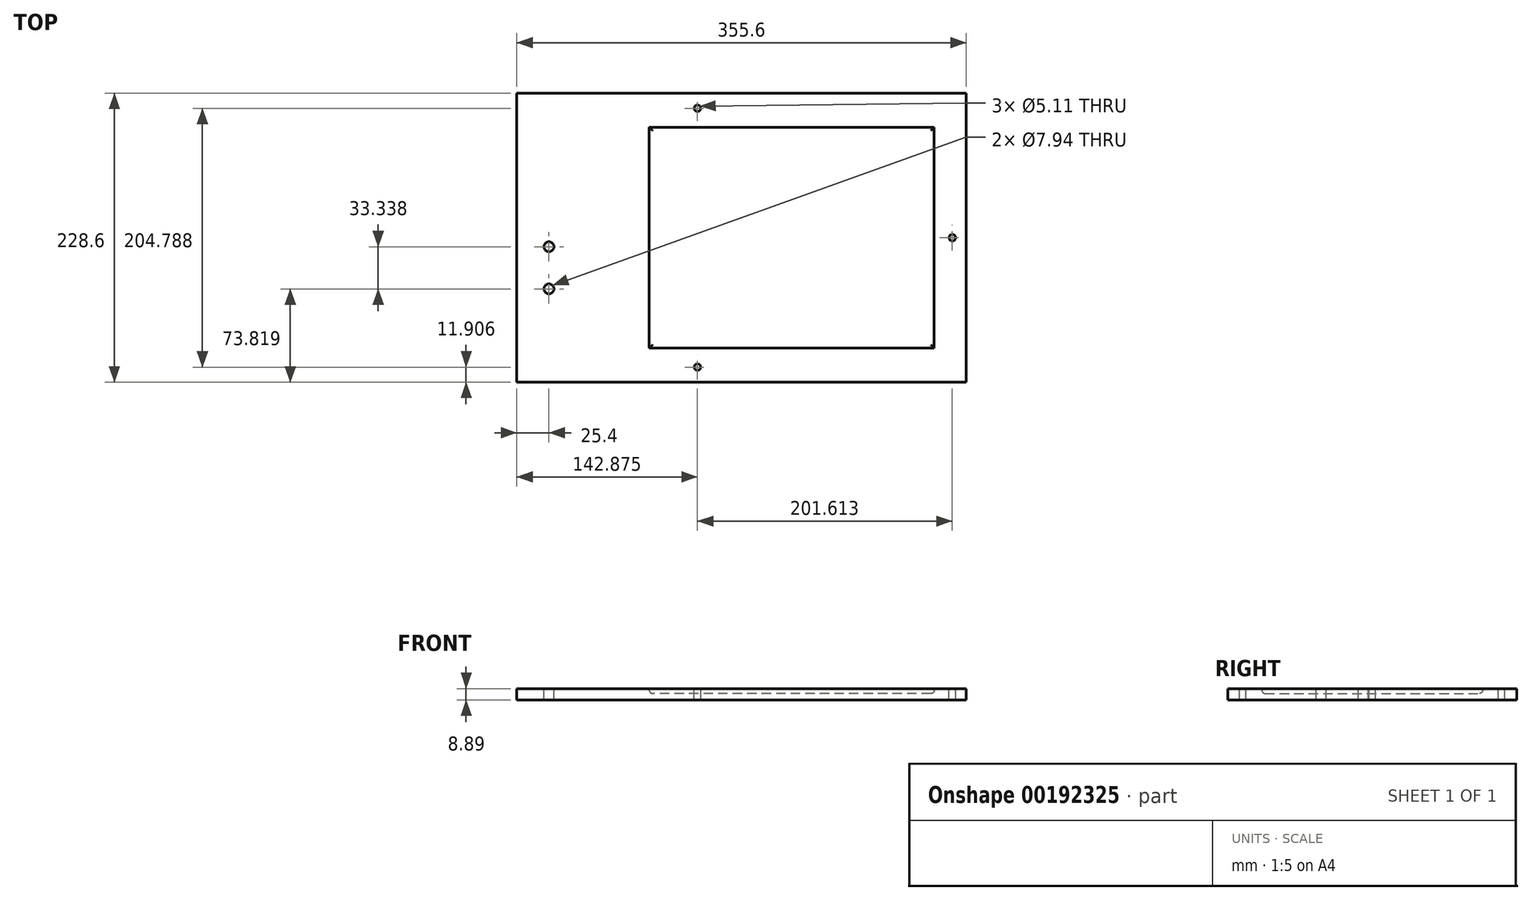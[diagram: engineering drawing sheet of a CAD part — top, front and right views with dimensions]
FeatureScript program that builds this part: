
annotation { "Feature Type Name" : "Feature", "Feature Type Description" : "" }
export const myFeature = defineFeature(function(context is Context, id is Id, definition is map)
    precondition{}
    {
        {
            var Q0;
            Q0=qCreatedBy(makeId("Top.planeOp"),FACE);
            var sketch = newSketch(context, id + "F0", { "sketchPlane" : qUnion([Q0])});
            skLineSegment(sketch, "E0.bottom", {"start": v(-177.8, 114.3) * mm, "end": v(177.8, 114.3) * mm});
            skLineSegment(sketch, "E0.top", {"start": v(-177.8, -114.3) * mm, "end": v(177.8, -114.3) * mm});
            skLineSegment(sketch, "E0.left", {"start": v(-177.8, 114.3) * mm, "end": v(-177.8, -114.3) * mm});
            skLineSegment(sketch, "E0.right", {"start": v(177.8, 114.3) * mm, "end": v(177.8, -114.3) * mm});
            skPoint(sketch, "E0.middle", {"position": v(0, 0) * mm});
            skSolve(sketch);
        }
        {
            var Q0;
            Q0 = qSketchRegion(id + "F0", true);
            extrude(context, id + "F1", {"entities" : qUnion([Q0]), "depth" : 8.9 * mm});
        }
        {
            var Q0;
            Q0=makeQuery(id+"F1.opExtrude","CAP_FACE",FACE,{"disambiguationData":[OSD([sQuery(id+"F0.wireOp",EDGE,"E0.bottom"),sQuery(id+"F0.wireOp",EDGE,"E0.top"),sQuery(id+"F0.wireOp",EDGE,"E0.left"),sQuery(id+"F0.wireOp",EDGE,"E0.right")])],"isStart":false});
            var sketch = newSketch(context, id + "F2", { "sketchPlane" : qUnion([Q0])});
            skLineSegment(sketch, "E1.bottom", {"start": v(152.4, -87.31) * mm, "end": v(-73.03, -87.31) * mm});
            skLineSegment(sketch, "E1.top", {"start": v(152.4, 87.31) * mm, "end": v(-73.03, 87.31) * mm});
            skLineSegment(sketch, "E1.left", {"start": v(152.4, -87.31) * mm, "end": v(152.4, 87.31) * mm});
            skLineSegment(sketch, "E1.right", {"start": v(-73.03, -87.31) * mm, "end": v(-73.03, 87.31) * mm});
            skLineSegment(sketch, "E2", {"start": v(152.4, 0) * mm, "end": v(298.72, 0) * mm, "construction": true});
            skSolve(sketch);
        }
        {
            var Q0;
            Q0 = qSketchRegion(id + "F2", true);
            extrude(context, id + "F3", {"entities" : qUnion([Q0]), "operationType" : NewBodyOperationType.REMOVE, "oppositeDirection" : true, "depth" : 3.8 * mm});
        }
        {
            var Q0;
            Q0=makeQuery(id+"F3.boolean.opBoolean","COPY",FACE,{"derivedFrom":makeQuery(id+"F3.opExtrude","CAP_FACE",FACE,{"disambiguationData":[OSD([sQuery(id+"F2.wireOp",EDGE,"E1.bottom"),sQuery(id+"F2.wireOp",EDGE,"E1.top"),sQuery(id+"F2.wireOp",EDGE,"E1.left"),sQuery(id+"F2.wireOp",EDGE,"E1.right")])],"isStart":false})});
            fillet(context, id + "F4", {"entities" : qUnion([Q0]), "radius" : 2.54 * mm, "tangentPropagation" : true, "allowEdgeOverflow" : false});
        }
        {
            var Q0;
            Q0=makeQuery(id+"F1.opExtrude","CAP_FACE",FACE,{"disambiguationData":[OSD([sQuery(id+"F0.wireOp",EDGE,"E0.bottom"),sQuery(id+"F0.wireOp",EDGE,"E0.top"),sQuery(id+"F0.wireOp",EDGE,"E0.left"),sQuery(id+"F0.wireOp",EDGE,"E0.right")])],"isStart":false});
            var sketch = newSketch(context, id + "F5", { "sketchPlane" : qUnion([Q0])});
            skLineSegment(sketch, "E3", {"start": v(0, 0) * mm, "end": v(177.8, 0) * mm, "construction": true});
            skPoint(sketch, "E4", {"position": v(166.69, 0) * mm});
            skLineSegment(sketch, "E5", {"start": v(177.8, 0) * mm, "end": v(-34.93, 0) * mm, "construction": true});
            skPoint(sketch, "E5.endSnap0", {"position": v(152.4, 0) * mm});
            skLineSegment(sketch, "E6", {"start": v(-34.93, 114.3) * mm, "end": v(-34.93, -114.3) * mm, "construction": true});
            skPoint(sketch, "E7", {"position": v(-34.93, 102.4) * mm});
            skPoint(sketch, "E8", {"position": v(-34.93, -102.4) * mm});
            skSolve(sketch);
        }
        {
            var Q0;
            Q0=sQuery(id+"F5.wireOp",VERTEX,"E8");
            var Q1;
            Q1=sQuery(id+"F5.wireOp",VERTEX,"E7");
            var Q2;
            Q2=sQuery(id+"F5.wireOp",VERTEX,"E4");
            var Q3;
            Q3=makeQuery(id+"F1.opExtrude","SWEPT_BODY",BODY,{"disambiguationData":[OSD([sQuery(id+"F0.wireOp",EDGE,"E0.bottom"),sQuery(id+"F0.wireOp",EDGE,"E0.top"),sQuery(id+"F0.wireOp",EDGE,"E0.left"),sQuery(id+"F0.wireOp",EDGE,"E0.right")])]});
            hole(context, id + "F6", {"style" : HoleStyle.SIMPLE, "endStyle" : HoleEndStyle.THROUGH, "standardTappedOrClearance" : lookupTablePath({ "standard" : "ANSI", "fit" : "Normal (ASME)", "size" : "#10", "type" : "Clearance" }), "standardBlindInLast" : lookupTablePath({ "fit" : "Free", "standard" : "ANSI", "size" : "#10", "type" : "Clearance" }), "holeDiameter" : 5.1 * mm, "locations" : qUnion([Q0, Q1, Q2]), "scope" : qUnion([Q3]), "isTappedThrough" : true});
        }
        {
            var Q0;
            Q0=makeQuery(id+"F1.opExtrude","CAP_FACE",FACE,{"disambiguationData":[OSD([sQuery(id+"F0.wireOp",EDGE,"E0.bottom"),sQuery(id+"F0.wireOp",EDGE,"E0.top"),sQuery(id+"F0.wireOp",EDGE,"E0.left"),sQuery(id+"F0.wireOp",EDGE,"E0.right")])],"isStart":false});
            var sketch = newSketch(context, id + "F7", { "sketchPlane" : qUnion([Q0])});
            skPoint(sketch, "E9", {"position": v(-152.4, -40.48) * mm});
            skPoint(sketch, "E10", {"position": v(-152.4, -7.14) * mm});
            skLineSegment(sketch, "E11", {"start": v(-73.03, -23.81) * mm, "end": v(-152.4, -23.81) * mm, "construction": true});
            skLineSegment(sketch, "E12", {"start": v(-152.4, -7.14) * mm, "end": v(-152.4, -40.48) * mm, "construction": true});
            skSolve(sketch);
        }
        {
            var Q0;
            Q0=sQuery(id+"F7.wireOp",VERTEX,"E10");
            var Q1;
            Q1=sQuery(id+"F7.wireOp",VERTEX,"E9");
            var Q2;
            Q2=makeQuery(id+"F1.opExtrude","SWEPT_BODY",BODY,{"disambiguationData":[OSD([sQuery(id+"F0.wireOp",EDGE,"E0.bottom"),sQuery(id+"F0.wireOp",EDGE,"E0.top"),sQuery(id+"F0.wireOp",EDGE,"E0.left"),sQuery(id+"F0.wireOp",EDGE,"E0.right")])]});
            hole(context, id + "F8", {"style" : HoleStyle.SIMPLE, "endStyle" : HoleEndStyle.THROUGH, "standardTappedOrClearance" : lookupTablePath({ "standard" : "ANSI", "engagement" : "75%", "pitch" : "16 tpi", "size" : "3/8", "type" : "Tapped" }), "standardBlindInLast" : lookupTablePath({ "standard" : "ANSI", "engagement" : "75%", "pitch" : "16 tpi", "size" : "3/8", "type" : "Tapped" }), "holeDiameter" : 7.94 * mm, "locations" : qUnion([Q0, Q1]), "scope" : qUnion([Q2]), "isTappedThrough" : true, "majorDiameter" : 9.53 * mm, "showTappedDepth" : true});
        }
    });
